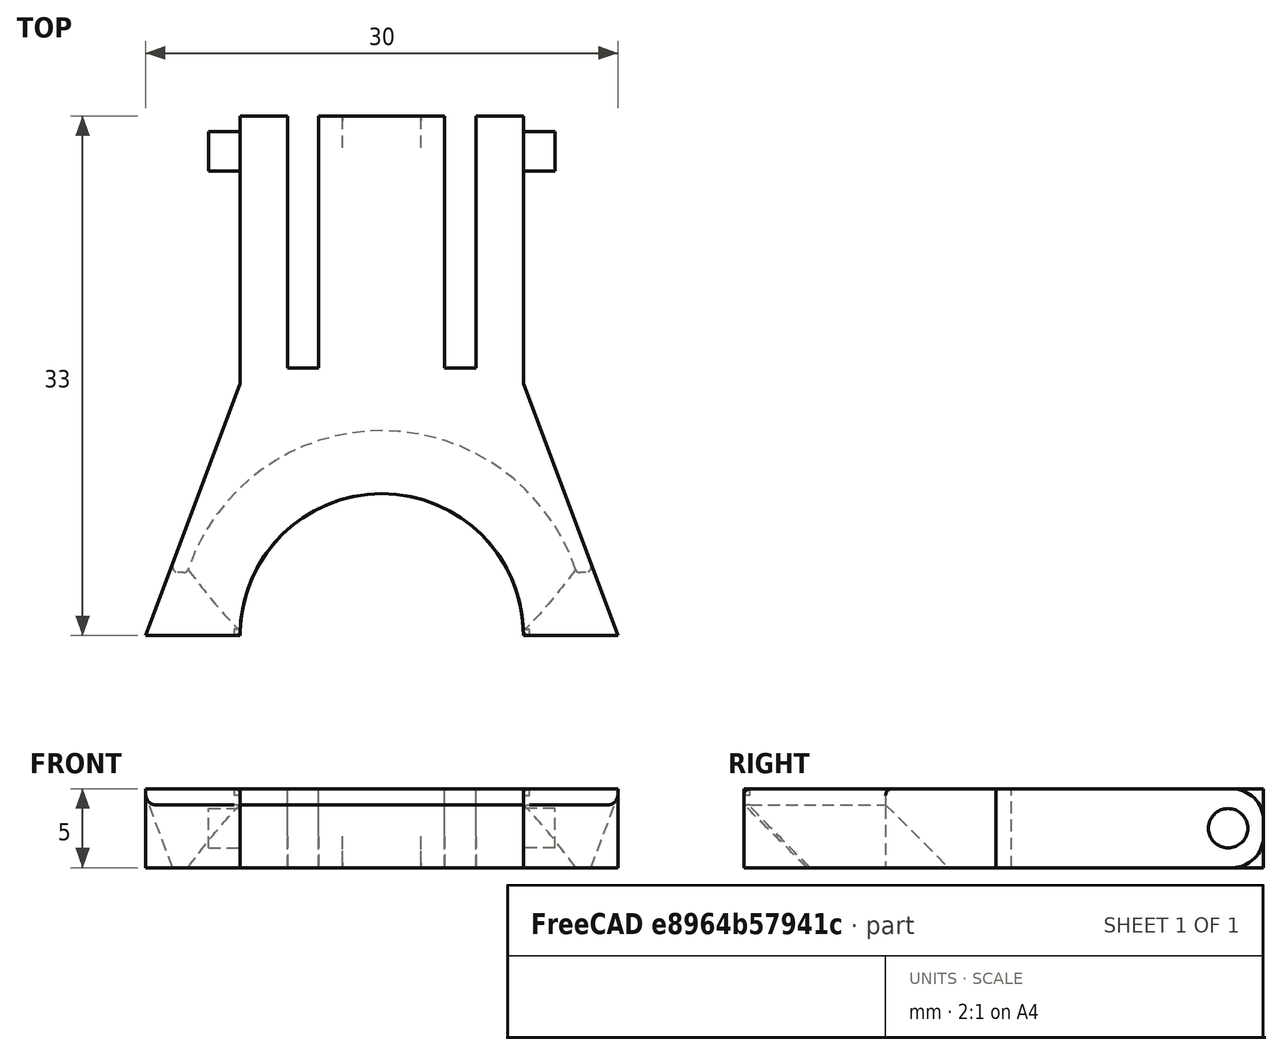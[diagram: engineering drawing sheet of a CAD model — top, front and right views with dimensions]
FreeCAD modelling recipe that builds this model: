
FCSTD DOCUMENT  (FreeCAD 0.19R24276 (Git))
Label: patillaBaseRefrigeradora
License: All rights reserved
LicenseURL: http://en.wikipedia.org/wiki/All_rights_reserved
objects: TechDraw::DrawViewDimension×13, Part::Fillet×6, Part::MultiFuse×3, TechDraw::DrawProjGroupItem×3, TechDraw::DrawSVGTemplate×2, TechDraw::DrawViewPart×2, TechDraw::DrawPage×2, Sketcher::SketchObject×1, PartDesign::Pad×1, PartDesign::Body×1, Part::Cylinder×1, Part::Mirroring×1, Part::Box×1, Part::Chamfer×1, TechDraw::DrawProjGroup×1, TechDraw::DrawViewAnnotation×1
note: 17 computed .brp shape members not serialized (recipe doc carries the construction recipe); baked Part::Feature solids carry a one-line shape summary decoded from their .brp

FEATURE [Sketcher::SketchObject] Sketch
  FullyConstrained = false
  MapMode = 5
  Support = -> [XY_Plane]
  sketch-geometry (16):
    g0: ArcOfCircle CenterX=0 CenterY=0 CenterZ=0 NormalX=0 NormalY=0 NormalZ=1 AngleXU=0 Radius=9 StartAngle=0 EndAngle=3.14159
    g1: LineSegment StartX=-9 StartY=1.1e-15 StartZ=0 EndX=-15 EndY=1.1e-15 EndZ=0
    g2: LineSegment StartX=-15 StartY=1.1e-15 StartZ=0 EndX=-9 EndY=16 EndZ=0
    g3: LineSegment StartX=-9 StartY=16 StartZ=0 EndX=-9 EndY=33 EndZ=0
    g4: LineSegment StartX=9 StartY=33 StartZ=0 EndX=9 EndY=16 EndZ=0
    g5: LineSegment StartX=9 StartY=16 StartZ=0 EndX=15 EndY=1.8e-15 EndZ=0
    g6: LineSegment StartX=15 StartY=0 StartZ=0 EndX=9 EndY=0 EndZ=0
    g7: LineSegment StartX=-9 StartY=33 StartZ=0 EndX=-6 EndY=33 EndZ=0
    g8: LineSegment StartX=-6 StartY=33 StartZ=0 EndX=-6 EndY=17 EndZ=0
    g9: LineSegment StartX=-6 StartY=17 StartZ=0 EndX=-4 EndY=17 EndZ=0
    g10: LineSegment StartX=-4 StartY=17 StartZ=0 EndX=-4 EndY=33 EndZ=0
    g11: LineSegment StartX=-4 StartY=33 StartZ=0 EndX=4 EndY=33 EndZ=0
    g12: LineSegment StartX=4 StartY=33 StartZ=0 EndX=4 EndY=17 EndZ=0
    g13: LineSegment StartX=4 StartY=17 StartZ=0 EndX=6 EndY=17 EndZ=0
    g14: LineSegment StartX=6 StartY=17 StartZ=0 EndX=6 EndY=33 EndZ=0
    g15: LineSegment StartX=6 StartY=33 StartZ=0 EndX=9 EndY=33 EndZ=0
  constraints (47):
    c: Coincident(g0,g-1)
    c: Diameter(g0) = 18
    c: PointOnObject(g1,g-1)
    c: Horizontal(g1)
    c: Coincident(g1,g2)
    c: Coincident(g2,g3)
    c: Vertical(g3)
    c: Vertical(g4)
    c: Coincident(g4,g5)
    c: PointOnObject(g5,g-1)
    c: Coincident(g5,g6)
    c: Horizontal(g6)
    c: Equal(g6,g1)
    c: Symmetric(g2,g4,g-2)
    c: DistanceY(g4,g4) = 17
    c: Coincident(g3,g7)
    c: Horizontal(g7)
    c: Coincident(g7,g8)
    c: Vertical(g8)
    c: Coincident(g8,g9)
    c: Horizontal(g9)
    c: Coincident(g9,g10)
    c: Vertical(g10)
    c: Coincident(g10,g11)
    c: Horizontal(g11)
    c: Coincident(g11,g12)
    c: Vertical(g12)
    c: Coincident(g12,g13)
    c: Coincident(g13,g14)
    c: Vertical(g14)
    c: Coincident(g14,g15)
    c: Coincident(g15,g4)
    c: Horizontal(g15)
    c: Horizontal(g13)
    c: Equal(g7,g15)
    c: DistanceX(g7,g7) = 3
    c: DistanceX(g11,g11) = 8
    c: DistanceX(g2,g4) = 18
    c: Equal(g3,g4)
    c: Equal(g10,g12)
    c: Equal(g10,g8)
    c: Equal(g9,g13)
    c: DistanceY(g12,g12) = 16
    c: Coincident(g0,g6)
    c: Coincident(g0,g1)
    c: DistanceX(g1,g1) = 6
    c: DistanceY(g0,g2) = 16
FEATURE [PartDesign::Pad] Pad
  AllowMultiFace = false
  Direction = (1,1,1)
  Length = 5
  Length2 = 100
  Profile = -> Sketch
  Type = 0
FEATURE [PartDesign::Body] Body
  Group = -> [Sketch,Pad]
  Origin = -> Origin
  Tip = -> Pad
FEATURE [Part::Cylinder] Cylinder
  Angle = 360
  AttacherType = Attacher::AttachEngine3D
  Height = 2
  Placement = pos=(-11,31.75,2.5) rot=(0,1,0;1.5708rad)
  Radius = 1.25
FEATURE [Part::Mirroring] Part__Mirroring  label="Cylinder (Mirror #1)"
  Base = (0,0,0)
  Normal = (1,0,0)
  Source = -> Cylinder
FEATURE [Part::Box] Box  label="Cube"
  AttacherType = Attacher::AttachEngine3D
  Height = 3
  Length = 5
  Placement = pos=(-2.5,30,0) rot=(0,0,1;0rad)
  Width = 3
FEATURE [Part::Fillet] Fillet
  Base = -> Pad
  Edges = 6 edges r=2: [Edge15,Edge16,Edge27,Edge28,Edge39,Edge40]
FEATURE [Part::Fillet] Fillet001
  Base = -> Box
  Edges = 1 edges r=0.3: [Edge11]
FEATURE [Part::Chamfer] Chamfer
  Base = -> Fillet
  Edges = 3 edges r=4: [Edge16,Edge18,Edge20]
FEATURE [Part::Fillet] Fillet002
  Base = -> Chamfer
  Edges = 2 edges r=0.4: [Edge64,Edge67]
FEATURE [Part::Fillet] Fillet003
  Base = -> Fillet002
  Edges = 2 edges r=0.4: [Edge3,Edge57]
FEATURE [Part::Fillet] Fillet004
  Base = -> Fillet003
  Edges = 2 edges r=0.4: [Edge51,Edge80]
FEATURE [Part::Fillet] Fillet005
  Base = -> Fillet004
  Edges = 1 edges r=0.4: [Edge83]
FEATURE [Part::MultiFuse] Fusion
  Placement = pos=(0,-1,0) rot=(0,0,1;0rad)
  Shapes = -> [Part__Mirroring,Cylinder]
FEATURE [Part::MultiFuse] Fusion001
  Shapes = -> [Fillet005,Fillet001]
FEATURE [Part::MultiFuse] Fusion002
  Shapes = -> [Fusion,Fusion001]
FEATURE [TechDraw::DrawSVGTemplate] Template
  EditableTexts = Designed_by_Name=<owner>; Drawing_number=001; FC-Date=-; FC-SC=1:1; FC-SH=1/2; FC-Title=Laptop Base Clip; Subtitle=Patilla Base Laptop; Weight=<10gr
  Height = 210
  Orientation = 1
  Width = 297
FEATURE [TechDraw::DrawSVGTemplate] Template001
  EditableTexts = Designed_by_Name=<owner>; Drawing_number=001; FC-Date=-; FC-SC=3:1; FC-SH=2/2; FC-Title=Laptop Base Clip; Subtitle=Patilla Base Laptop; Weight=<10gr
  Height = 210
  Orientation = 1
  Width = 297
FEATURE [TechDraw::DrawViewPart] View
  CoarseView = false
  Direction = (0.577,-0.577,0.577)
  Focus = 100
  HardHidden = false
  IsoCount = 0
  IsoHidden = false
  IsoVisible = false
  LockPosition = false
  Perspective = false
  Rotation = 0
  Scale = 3
  ScaleType = 0
  SeamHidden = false
  SeamVisible = true
  SmoothHidden = false
  SmoothVisible = true
  Source = -> [Fusion002]
  X = 209.669
  XDirection = (0.707,0.707,0)
  Y = 130.325
FEATURE [TechDraw::DrawProjGroupItem] ProjItem  label="Front"
  CoarseView = false
  Direction = (0,-1,0)
  Focus = 100
  HardHidden = false
  IsoCount = 0
  IsoHidden = false
  IsoVisible = false
  LockPosition = true
  Perspective = false
  Rotation = 0
  RotationVector = (1,0,0)
  ScaleType = 2
  SeamHidden = false
  SeamVisible = true
  SmoothHidden = false
  SmoothVisible = true
  Source = -> [Fusion002]
  Type = 0
  X = 0
  XDirection = (1,0,0)
  Y = 0
FEATURE [TechDraw::DrawProjGroupItem] ProjItem001  label="Right"
  CoarseView = false
  Direction = (1,-1e-16,0)
  Focus = 100
  HardHidden = false
  IsoCount = 0
  IsoHidden = false
  IsoVisible = false
  LockPosition = false
  Perspective = false
  Rotation = 0
  RotationVector = (1,0,0)
  ScaleType = 2
  SeamHidden = false
  SeamVisible = true
  SmoothHidden = false
  SmoothVisible = true
  Source = -> [Fusion002]
  Type = 2
  X = -48.206
  XDirection = (1e-16,1,0)
  Y = 0
FEATURE [TechDraw::DrawProjGroupItem] ProjItem002  label="Top"
  CoarseView = false
  Direction = (0,0,1)
  Focus = 100
  HardHidden = false
  IsoCount = 0
  IsoHidden = false
  IsoVisible = false
  LockPosition = false
  Perspective = false
  Rotation = 0
  RotationVector = (1,0,0)
  ScaleType = 2
  SeamHidden = false
  SeamVisible = true
  SmoothHidden = false
  SmoothVisible = true
  Source = -> [Fusion002]
  Type = 4
  X = 0
  XDirection = (1,0,0)
  Y = -48.0522
FEATURE [TechDraw::DrawProjGroup] ProjGroup
  Anchor = -> ProjItem
  AutoDistribute = true
  LockPosition = false
  ProjectionType = 0
  Rotation = 0
  ScaleType = 2
  Source = -> [Fusion002]
  Views = -> [ProjItem,ProjItem001,ProjItem002]
  X = 99.4091
  Y = 166.948
  spacingX = 15
  spacingY = 15
FEATURE [TechDraw::DrawViewDimension] Dimension
  Arbitrary = false
  ArbitraryTolerances = false
  EqualTolerance = true
  FormatSpec = %.2f
  FormatSpecOverTolerance = %+.2f
  FormatSpecUnderTolerance = %+.2f
  Inverted = false
  LockPosition = false
  MeasureType = 1
  OverTolerance = 0
  References2D = -> [ProjItem002]
  Rotation = 0
  ScaleType = 0
  TheoreticalExact = false
  Type = 1
  UnderTolerance = 0
  X = 1.20064
  Y = -31.2163
FEATURE [TechDraw::DrawViewDimension] Dimension001
  Arbitrary = false
  ArbitraryTolerances = false
  EqualTolerance = true
  FormatSpec = %.2f
  FormatSpecOverTolerance = %+.2f
  FormatSpecUnderTolerance = %+.2f
  Inverted = false
  LockPosition = false
  MeasureType = 1
  OverTolerance = 0
  References2D = -> [ProjItem002]
  Rotation = 0
  ScaleType = 0
  TheoreticalExact = false
  Type = 2
  UnderTolerance = 0
  X = -37.0381
  Y = -0.137086
FEATURE [TechDraw::DrawViewDimension] Dimension002
  Arbitrary = false
  ArbitraryTolerances = false
  EqualTolerance = true
  FormatSpec = ⌀%.2f
  FormatSpecOverTolerance = %+.2f
  FormatSpecUnderTolerance = %+.2f
  Inverted = false
  LockPosition = false
  MeasureType = 1
  OverTolerance = 0
  References2D = -> [ProjItem002]
  Rotation = 0
  ScaleType = 0
  TheoreticalExact = false
  Type = 5
  UnderTolerance = 0
  X = 27.2717
  Y = 11.6634
FEATURE [TechDraw::DrawViewDimension] Dimension003
  Arbitrary = false
  ArbitraryTolerances = false
  EqualTolerance = true
  FormatSpec = %.2f
  FormatSpecOverTolerance = %+.2f
  FormatSpecUnderTolerance = %+.2f
  Inverted = false
  LockPosition = false
  MeasureType = 1
  OverTolerance = 0
  References2D = -> [ProjItem]
  Rotation = 0
  ScaleType = 0
  TheoreticalExact = false
  Type = 2
  UnderTolerance = 0
  X = 17.0329
  Y = -13.283
FEATURE [TechDraw::DrawViewDimension] Dimension004
  Arbitrary = false
  ArbitraryTolerances = false
  EqualTolerance = true
  FormatSpec = %.2f
  FormatSpecOverTolerance = %+.2f
  FormatSpecUnderTolerance = %+.2f
  Inverted = false
  LockPosition = false
  MeasureType = 1
  OverTolerance = 0
  References2D = -> [ProjItem002]
  Rotation = 0
  ScaleType = 0
  TheoreticalExact = false
  Type = 1
  UnderTolerance = 0
  X = -4.16889
  Y = 29.0141
FEATURE [TechDraw::DrawPage] Page  label="Vistas"
  KeepUpdated = true
  NextBalloonIndex = 1
  ProjectionType = 0
  Template = -> Template
  Views = -> [View,ProjGroup,Dimension,Dimension001,Dimension002,Dimension003,Dimension004]
FEATURE [TechDraw::DrawViewPart] View001
  CoarseView = false
  Direction = (0.577,-0.577,0.577)
  Focus = 100
  HardHidden = false
  IsoCount = 0
  IsoHidden = false
  IsoVisible = false
  LockPosition = false
  Perspective = false
  Rotation = 0
  Scale = 3
  ScaleType = 0
  SeamHidden = false
  SeamVisible = true
  SmoothHidden = false
  SmoothVisible = true
  Source = -> [Fusion002]
  X = 144.458
  XDirection = (0.707,0.707,0)
  Y = 127.883
FEATURE [TechDraw::DrawViewDimension] Dimension005
  Arbitrary = false
  ArbitraryTolerances = false
  EqualTolerance = true
  FormatSpec = %.2f
  FormatSpecOverTolerance = %+.2f
  FormatSpecUnderTolerance = %+.2f
  Inverted = false
  LockPosition = false
  MeasureType = 1
  OverTolerance = 0
  References2D = -> [View001]
  Rotation = 0
  Scale = 3
  ScaleType = 0
  TheoreticalExact = false
  Type = 0
  UnderTolerance = 0
  X = 2.7536
  Y = 55.1891
FEATURE [TechDraw::DrawViewDimension] Dimension006
  Arbitrary = false
  ArbitraryTolerances = false
  EqualTolerance = true
  FormatSpec = %.2f
  FormatSpecOverTolerance = %+.2f
  FormatSpecUnderTolerance = %+.2f
  Inverted = false
  LockPosition = false
  MeasureType = 1
  OverTolerance = 0
  References2D = -> [View001]
  Rotation = 0
  Scale = 3
  ScaleType = 0
  TheoreticalExact = false
  Type = 0
  UnderTolerance = 0
  X = 49.8802
  Y = 34.5117
FEATURE [TechDraw::DrawViewDimension] Dimension007
  Arbitrary = false
  ArbitraryTolerances = false
  EqualTolerance = true
  FormatSpec = %.2f
  FormatSpecOverTolerance = %+.2f
  FormatSpecUnderTolerance = %+.2f
  Inverted = false
  LockPosition = false
  MeasureType = 1
  OverTolerance = 0
  References2D = -> [View001]
  Rotation = 0
  Scale = 3
  ScaleType = 0
  TheoreticalExact = false
  Type = 0
  UnderTolerance = 0
  X = 1.77251
  Y = 6.72588
FEATURE [TechDraw::DrawViewDimension] Dimension008
  Arbitrary = false
  ArbitraryTolerances = false
  EqualTolerance = true
  FormatSpec = ⌀%.2f
  FormatSpecOverTolerance = %+.2f
  FormatSpecUnderTolerance = %+.2f
  Inverted = false
  LockPosition = false
  MeasureType = 1
  OverTolerance = 0
  References2D = -> [View001]
  Rotation = 0
  Scale = 3
  ScaleType = 0
  TheoreticalExact = false
  Type = 5
  UnderTolerance = 0
  X = 77.5632
  Y = 12.1467
FEATURE [TechDraw::DrawViewDimension] Dimension009
  Arbitrary = false
  ArbitraryTolerances = false
  EqualTolerance = true
  FormatSpec = %.2f
  FormatSpecOverTolerance = %+.2f
  FormatSpecUnderTolerance = %+.2f
  Inverted = false
  LockPosition = false
  MeasureType = 1
  OverTolerance = 0
  References2D = -> [View001]
  Rotation = 0
  Scale = 3
  ScaleType = 0
  TheoreticalExact = false
  Type = 0
  UnderTolerance = 0
  X = 72.4487
  Y = 57.2098
FEATURE [TechDraw::DrawViewDimension] Dimension010
  Arbitrary = false
  ArbitraryTolerances = false
  EqualTolerance = true
  FormatSpec = %.2f
  FormatSpecOverTolerance = %+.2f
  FormatSpecUnderTolerance = %+.2f
  Inverted = false
  LockPosition = false
  MeasureType = 1
  OverTolerance = 0
  References2D = -> [View001]
  Rotation = 0
  Scale = 3
  ScaleType = 0
  TheoreticalExact = false
  Type = 0
  UnderTolerance = 0
  X = -61.9439
  Y = 32.8012
FEATURE [TechDraw::DrawViewDimension] Dimension011
  Arbitrary = false
  ArbitraryTolerances = false
  EqualTolerance = true
  FormatSpec = %.2f
  FormatSpecOverTolerance = %+.2f
  FormatSpecUnderTolerance = %+.2f
  Inverted = false
  LockPosition = false
  MeasureType = 1
  OverTolerance = 0
  References2D = -> [View001]
  Rotation = 0
  Scale = 3
  ScaleType = 0
  TheoreticalExact = false
  Type = 0
  UnderTolerance = 0
  X = -69.5086
  Y = -12.2977
FEATURE [TechDraw::DrawViewDimension] Dimension012
  Arbitrary = false
  ArbitraryTolerances = false
  EqualTolerance = true
  FormatSpec = ⌀%.2f
  FormatSpecOverTolerance = %+.2f
  FormatSpecUnderTolerance = %+.2f
  Inverted = false
  LockPosition = false
  MeasureType = 1
  OverTolerance = 0
  References2D = -> [View001]
  Rotation = 0
  Scale = 3
  ScaleType = 0
  TheoreticalExact = false
  Type = 5
  UnderTolerance = 0
  X = 69.9874
  Y = 34.3161
FEATURE [TechDraw::DrawViewAnnotation] Annotation
  Font = osifont
  LineSpace = 80
  LockPosition = false
  MaxWidth = -1
  Rotation = 0
  Scale = 3
  ScaleType = 0
  Text = Aproximate measurements: | Check with 3D piece
  TextSize = 5
  TextStyle = 0
  X = 77.7
  Y = 69
FEATURE [TechDraw::DrawPage] Page001  label="Cotas"
  KeepUpdated = true
  NextBalloonIndex = 1
  ProjectionType = 0
  Scale = 3
  Template = -> Template001
  Views = -> [View001,Dimension005,Dimension006,Dimension007,Dimension008,Dimension009,Dimension010,Dimension011,Dimension012,Annotation]
